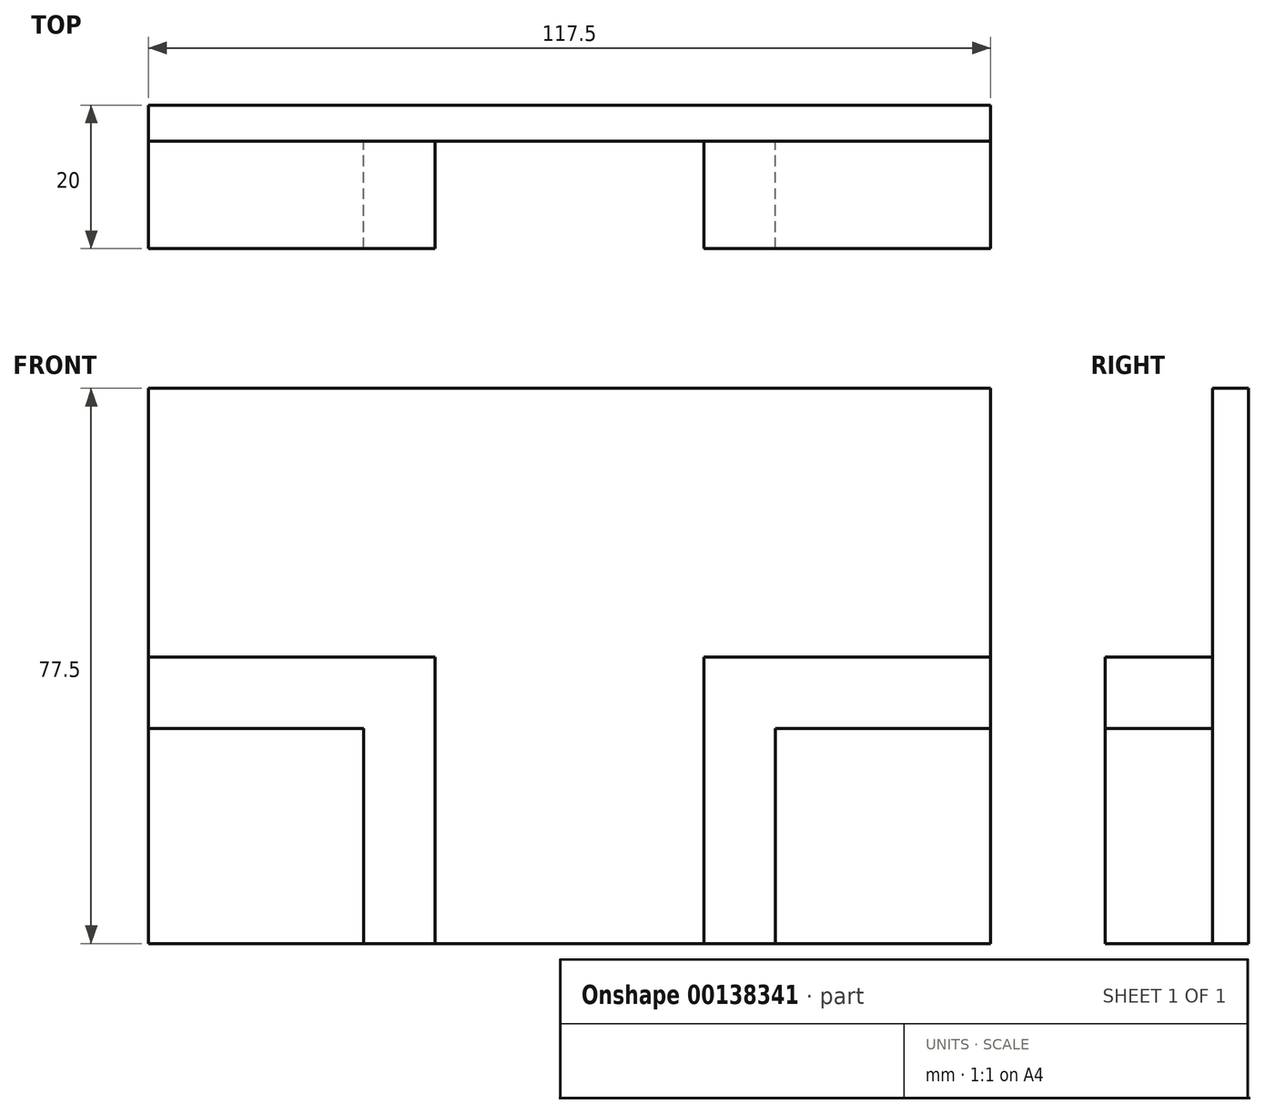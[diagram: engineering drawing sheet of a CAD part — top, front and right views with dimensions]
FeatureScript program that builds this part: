
annotation { "Feature Type Name" : "Feature", "Feature Type Description" : "" }
export const myFeature = defineFeature(function(context is Context, id is Id, definition is map)
    precondition{}
    {
        {
            var Q0;
            Q0=qCreatedBy(makeId("Front.planeOp"),FACE);
            var sketch = newSketch(context, id + "F0", { "sketchPlane" : qUnion([Q0])});
            skLineSegment(sketch, "E0", {"start": v(0, 0) * mm, "end": v(40, 0) * mm});
            skLineSegment(sketch, "E1", {"start": v(40, 0) * mm, "end": v(40, -10) * mm});
            skLineSegment(sketch, "E2", {"start": v(40, -10) * mm, "end": v(10, -10) * mm});
            skLineSegment(sketch, "E3", {"start": v(10, -10) * mm, "end": v(10, -40) * mm});
            skLineSegment(sketch, "E4", {"start": v(10, -40) * mm, "end": v(0, -40) * mm});
            skLineSegment(sketch, "E5", {"start": v(0, -40) * mm, "end": v(0, 0) * mm});
            skLineSegment(sketch, "E6", {"start": v(-18.75, 47.73) * mm, "end": v(-18.75, -62.1) * mm, "construction": true});
            skLineSegment(sketch, "E7.MirrorCS", {"start": v(-37.5, 0) * mm, "end": v(-77.5, 0) * mm});
            skLineSegment(sketch, "E8.MirrorCS", {"start": v(-77.5, 0) * mm, "end": v(-77.5, -10) * mm});
            skLineSegment(sketch, "E9.MirrorCS", {"start": v(-77.5, -10) * mm, "end": v(-47.5, -10) * mm});
            skLineSegment(sketch, "E10.MirrorCS", {"start": v(-47.5, -10) * mm, "end": v(-47.5, -40) * mm});
            skLineSegment(sketch, "E11.MirrorCS", {"start": v(-47.5, -40) * mm, "end": v(-37.5, -40) * mm});
            skLineSegment(sketch, "E12.MirrorCS", {"start": v(-37.5, -40) * mm, "end": v(-37.5, 0) * mm});
            skLineSegment(sketch, "E13.bottom", {"start": v(-23.75, 0) * mm, "end": v(-13.75, 0) * mm});
            skLineSegment(sketch, "E13.top", {"start": v(-23.75, 0) * mm, "end": v(-13.75, 0) * mm});
            skLineSegment(sketch, "E13.left", {"start": v(-23.75, 0) * mm, "end": v(-23.75, 0) * mm});
            skLineSegment(sketch, "E13.right", {"start": v(-13.75, 0) * mm, "end": v(-13.75, 0) * mm});
            skLineSegment(sketch, "E14", {"start": v(-23.75, 0) * mm, "end": v(-23.75, 37.5) * mm});
            skLineSegment(sketch, "E15", {"start": v(-23.75, 37.5) * mm, "end": v(-13.75, 37.5) * mm});
            skLineSegment(sketch, "E16", {"start": v(-13.75, 37.5) * mm, "end": v(-13.75, 0) * mm});
            skLineSegment(sketch, "E17", {"start": v(-77.5, 0) * mm, "end": v(-77.5, 37.5) * mm});
            skLineSegment(sketch, "E18", {"start": v(-77.5, 37.5) * mm, "end": v(-23.75, 37.5) * mm});
            skLineSegment(sketch, "E19", {"start": v(-13.75, 37.5) * mm, "end": v(40, 37.5) * mm});
            skLineSegment(sketch, "E20", {"start": v(40, 37.5) * mm, "end": v(40, 0) * mm});
            skLineSegment(sketch, "E21", {"start": v(-77.5, -10) * mm, "end": v(-77.5, -40) * mm});
            skLineSegment(sketch, "E22", {"start": v(-77.5, -40) * mm, "end": v(-47.5, -40) * mm});
            skLineSegment(sketch, "E23", {"start": v(-37.5, -40) * mm, "end": v(0, -40) * mm});
            skLineSegment(sketch, "E24", {"start": v(10, -40) * mm, "end": v(40, -40) * mm});
            skLineSegment(sketch, "E25", {"start": v(40, -40) * mm, "end": v(40, -10) * mm});
            skSolve(sketch);
        }
        {
            var Q0;
            Q0=makeQuery(id+"F0.imprint","IMPRINT",FACE,{"disambiguationData":[TD([[makeQuery(id+"F0.imprint","IMPRINT",EDGE,{"derivedFrom":sQuery(id+"F0.wireOp",EDGE,"E13.top")}),1.0]])]});
            var Q1;
            Q1=makeQuery(id+"F0.imprint","IMPRINT",FACE,{"disambiguationData":[TD([[makeQuery(id+"F0.imprint","IMPRINT",EDGE,{"derivedFrom":sQuery(id+"F0.wireOp",EDGE,"E0")}),-1.0]])]});
            var Q2;
            Q2=makeQuery(id+"F0.imprint","IMPRINT",FACE,{"disambiguationData":[TD([[makeQuery(id+"F0.imprint","IMPRINT",EDGE,{"derivedFrom":sQuery(id+"F0.wireOp",EDGE,"E7.MirrorCS")}),1.0]])]});
            extrude(context, id + "F1", {"entities" : qUnion([Q0, Q1, Q2]), "depth" : 15 * mm});
        }
        {
            var Q0;
            Q0 = qSketchRegion(id + "F0", true);
            extrude(context, id + "F2", {"entities" : qUnion([Q0]), "oppositeDirection" : true, "depth" : 5 * mm});
        }
    });
